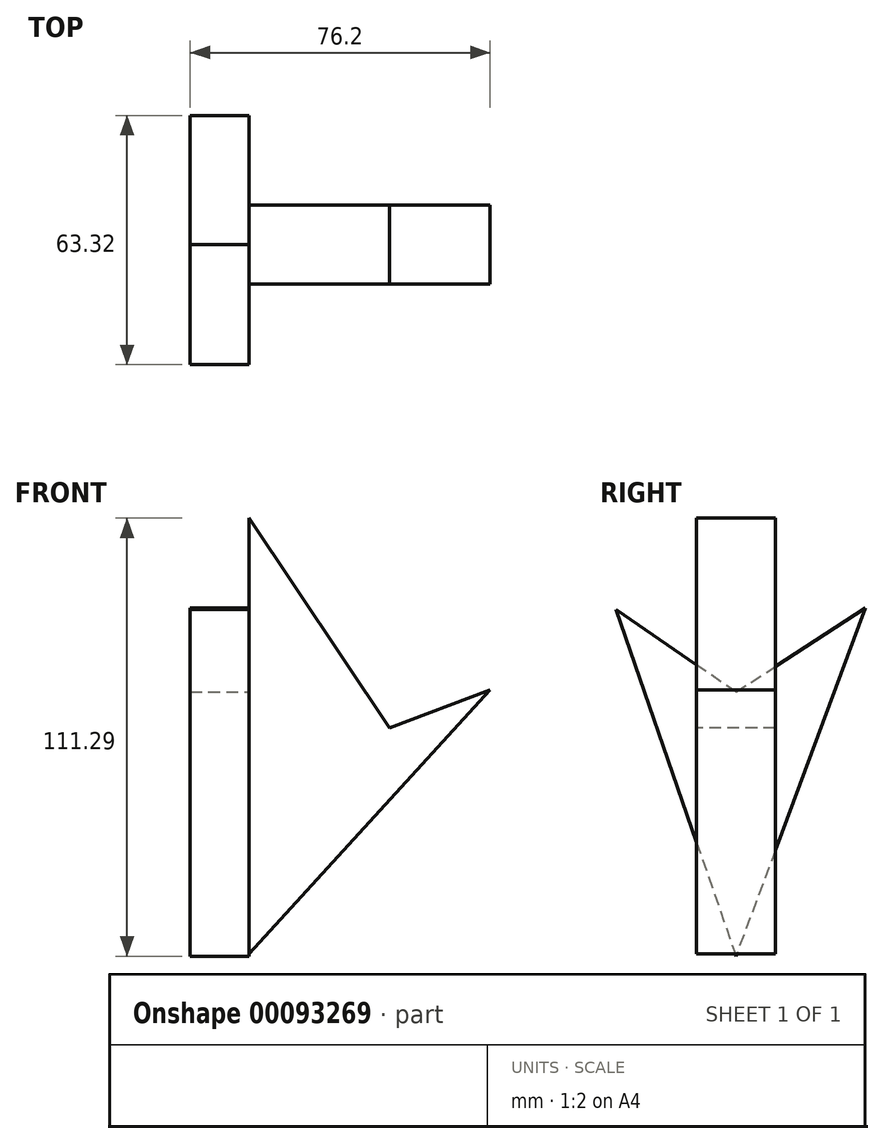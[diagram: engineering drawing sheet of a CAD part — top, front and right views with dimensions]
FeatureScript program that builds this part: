
annotation { "Feature Type Name" : "Feature", "Feature Type Description" : "" }
export const myFeature = defineFeature(function(context is Context, id is Id, definition is map)
    precondition{}
    {
        {
            var Q0;
            Q0=qCreatedBy(makeId("Front.planeOp"),FACE);
            var sketch = newSketch(context, id + "F0", { "sketchPlane" : qUnion([Q0])});
            skLineSegment(sketch, "E0", {"start": v(0, 53.34) * mm, "end": v(35.66, 0) * mm});
            skLineSegment(sketch, "E1", {"start": v(35.66, 0) * mm, "end": v(61.2, 9.69) * mm});
            skLineSegment(sketch, "E2", {"start": v(61.2, 9.69) * mm, "end": v(0, -57.41) * mm});
            skPoint(sketch, "E3.start.orphan", {"position": v(-33.69, 0) * mm});
            skLineSegment(sketch, "E4", {"start": v(0, 53.34) * mm, "end": v(0, -57.41) * mm});
            skSolve(sketch);
        }
        {
            var Q0;
            Q0=qCreatedBy(makeId("Right.planeOp"),FACE);
            var sketch = newSketch(context, id + "F1", { "sketchPlane" : qUnion([Q0])});
            skLineSegment(sketch, "E5", {"start": v(0, 9.12) * mm, "end": v(32.85, 30.46) * mm});
            skLineSegment(sketch, "E6", {"start": v(32.85, 30.46) * mm, "end": v(0, -57.95) * mm});
            skLineSegment(sketch, "E7", {"start": v(0, 9.12) * mm, "end": v(-30.47, 30.1) * mm});
            skLineSegment(sketch, "E8", {"start": v(-30.47, 30.1) * mm, "end": v(0, -57.95) * mm});
            skSolve(sketch);
        }
        {
            var Q0;
            Q0=makeQuery(id+"F1.imprint","IMPRINT",FACE,{"disambiguationData":[TD([[makeQuery(id+"F1.imprint","IMPRINT",EDGE,{"derivedFrom":sQuery(id+"F1.wireOp",EDGE,"E5")}),-1.0]])]});
            extrude(context, id + "F2", {"entities" : qUnion([Q0]), "oppositeDirection" : true, "depth" : 15 * mm});
        }
        {
            var Q0;
            Q0=makeQuery(id+"F0.imprint","IMPRINT",FACE,{"disambiguationData":[TD([[makeQuery(id+"F0.imprint","IMPRINT",EDGE,{"derivedFrom":sQuery(id+"F0.wireOp",EDGE,"OlcIzjbw-9mzf-TipH-BuX9-XR0WhE9xYZA7")}),-1.0]])]});
            var Q1;
            Q1=makeQuery(id+"F0.imprint","IMPRINT",FACE,{"disambiguationData":[TD([[makeQuery(id+"F0.imprint","IMPRINT",EDGE,{"derivedFrom":sQuery(id+"F0.wireOp",EDGE,"E0")}),-1.0]])]});
            extrude(context, id + "F3", {"entities" : qUnion([Q0, Q1]), "operationType" : NewBodyOperationType.ADD, "oppositeDirection" : true, "depth" : 10 * mm, "hasSecondDirection" : true, "secondDirectionOppositeDirection" : false, "secondDirectionDepth" : 10 * mm});
        }
    });
